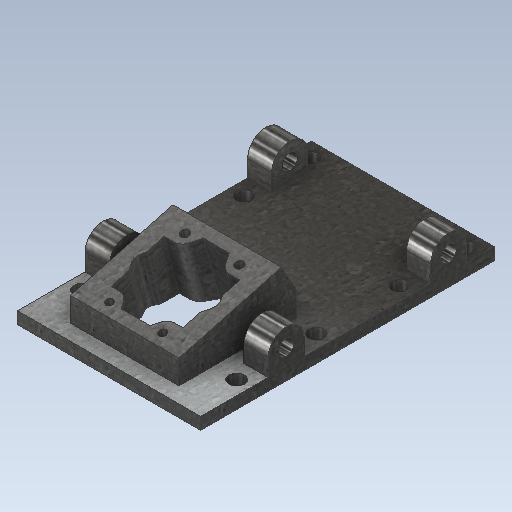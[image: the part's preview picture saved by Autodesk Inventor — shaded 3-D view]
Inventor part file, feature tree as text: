
AUTODESK INVENTOR PART (.ipt)
format: ipt  version: 2020 (Build 240168000, 168)  size: 400,384 bytes
history: native  units: mm
features: sketch x12, extrude x10, other x3, fillet x2, mirror x1, loft x1, projected_geometry x1
ambient origin geometry x8: Origin, YZ Plane, XZ Plane, XY Plane, X Axis, Y Axis, Z Axis, Center Point
bodies: Body1 (feature_tree)
feature tree (30):
  other  "Твердое тело1"
  extrude  "Выдавливание1"  Depth=244.0mm
  extrude  "Выдавливание2"  Depth=13.0mm
  extrude  "Выдавливание3"  Depth=20.0mm
  extrude  "Выдавливание4"  Depth=20.0mm
  fillet  "Сопряжение1"  Radius=10.0mm
  extrude  "Выдавливание5"  Depth=13.0mm
  extrude  "Выдавливание6"  Depth=20.0mm
  fillet  "Сопряжение2"  Radius=13.0mm
  extrude  "Выдавливание7"  Depth=13.0mm
  mirror  "Зеркальное отражение1"
  extrude  "Выдавливание8"  Depth=20.0mm
  other  "РабПлоскость1"
  loft  "Лофт1"
  other  "РабПлоскость2"
  extrude  "Extrusion11"  Depth=10.0mm TaperAngle=0.0deg
  extrude  "Extrusion12"  Depth=20.0mm
  sketch  "Эскиз1"
  sketch  "Эскиз2"
  sketch  "Эскиз3"
  sketch  "Эскиз4"
  sketch  "Эскиз5"
  sketch  "Эскиз6"
  sketch  "Эскиз7"
  sketch  "Эскиз8"
  sketch  "Эскиз9"
  sketch  "Эскиз10"
  projected_geometry  "Спроецированная петля1"
  sketch  "Sketch15"  dims[d0=152.0mm d1=244.0mm]
  sketch  "Sketch16"  dims[d2=10.0mm d3=0.0mm d4=13.0mm d5=11.5mm d6=41.5mm d7=10.0mm d8=0.0mm d9=13.0mm d10=11.5mm d11=13.0mm d12=13.0mm d13=11.5mm d14=11.5mm d15=10.0mm d16=0.0mm d17=107.5mm d18=69.0mm d19=12.5mm d20=30.0mm d21=20.0mm d24=28.0mm d25=29.0mm d26=0.0mm d27=15.0mm d28=13.0mm d29=29.0mm d30=0.0mm d31=20.0mm d32=30.0mm d34=53.0mm d35=29.0mm d36=0.0mm d37=15.0mm d38=13.0mm d39=29.0mm d40=0.0mm d41=98.0mm d42=90.0mm d43=13.0mm d44=20.0mm d45=0.0mm d46=-13.089969mm d47=88.0mm d48=0.0mm d49=90.0deg d50=0.0mm d51=90.0deg d54=22.5mm d55=45.0mm d57=22.5mm d59=21.0mm d76=88.0mm d77=85.0mm d78=61.5mm d79=0.0mm d80=88.0mm d81=85.0mm d82=61.5mm d83=0.0mm]
